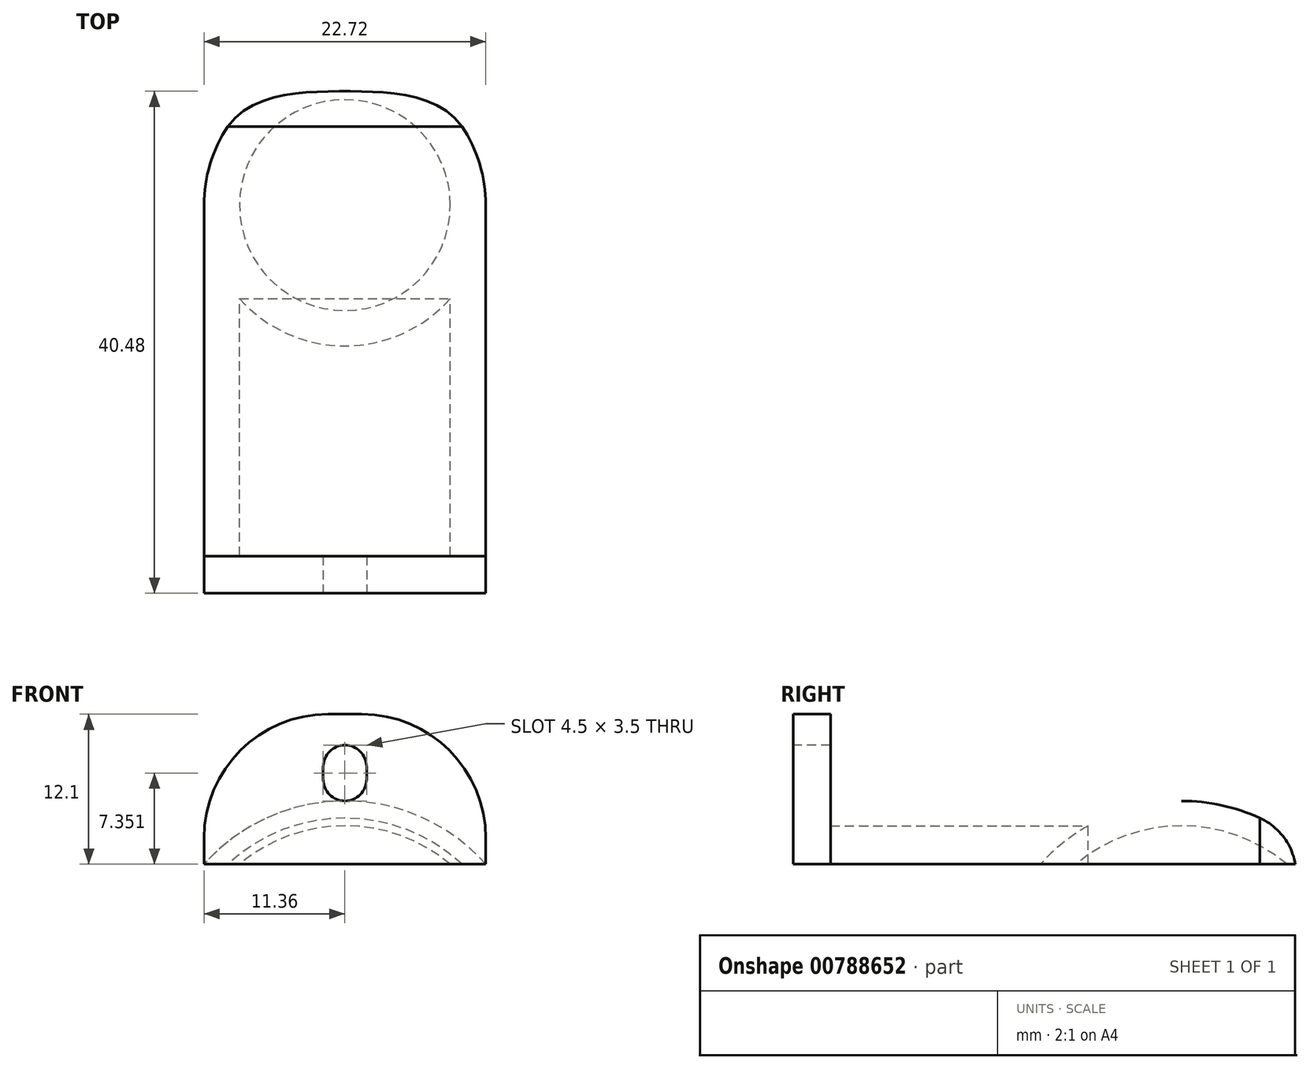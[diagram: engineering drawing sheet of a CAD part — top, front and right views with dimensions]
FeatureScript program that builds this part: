
annotation { "Feature Type Name" : "Feature", "Feature Type Description" : "" }
export const myFeature = defineFeature(function(context is Context, id is Id, definition is map)
    precondition{}
    {
        {
            var Q0;
            Q0=qCreatedBy(makeId("Front.planeOp"),FACE);
            var sketch = newSketch(context, id + "F0", { "sketchPlane" : qUnion([Q0])});
            skArc(sketch, "E0", {"start": v(8.5, 0) * mm, "mid": v(0, 3.1) * mm, "end": v(-8.5, 0) * mm});
            skLineSegment(sketch, "E1", {"start": v(-8.5, 0) * mm, "end": v(8.5, 0) * mm, "construction": true});
            skArc(sketch, "E2.0", {"start": v(11.36, 0) * mm, "mid": v(0, 5.1) * mm, "end": v(-11.36, 0) * mm});
            skLineSegment(sketch, "E3", {"start": v(-11.36, 0) * mm, "end": v(-8.5, 0) * mm});
            skLineSegment(sketch, "E4", {"start": v(8.5, 0) * mm, "end": v(11.36, 0) * mm});
            skLineSegment(sketch, "E5", {"start": v(-1.88, -10.1) * mm, "end": v(2.05, -10.1) * mm, "construction": true});
            skLineSegment(sketch, "E6.bottom", {"start": v(-11.36, 0) * mm, "end": v(11.36, 0) * mm});
            skLineSegment(sketch, "E6.top", {"start": v(-11.36, -4) * mm, "end": v(11.36, -4) * mm});
            skLineSegment(sketch, "E6.left", {"start": v(-11.36, 0) * mm, "end": v(-11.36, -4) * mm});
            skLineSegment(sketch, "E6.right", {"start": v(11.36, 0) * mm, "end": v(11.36, -4) * mm});
            skPoint(sketch, "E7", {"position": v(0, 5.1) * mm});
            skSolve(sketch);
        }
        {
            var Q0;
            Q0=makeQuery(id+"F0.imprint","IMPRINT",FACE,{"disambiguationData":[TD([[makeQuery(id+"F0.imprint","IMPRINT",EDGE,{"derivedFrom":sQuery(id+"F0.wireOp",EDGE,"E0")}),-1.0]])]});
            var Q1;
            Q1=sQuery(id+"F0.wireOp",EDGE,"E5");
            revolve(context, id + "F1", {"surfaceOperationType" : NewSurfaceOperationType.NEW, "entities" : qUnion([Q0]), "axis" : qUnion([Q1]), "revolveType" : RevolveType.SYMMETRIC, "angle" : 100 * degree});
        }
        {
            var Q0;
            Q0=makeQuery(id+"F0.imprint","IMPRINT",FACE,{"disambiguationData":[TD([[makeQuery(id+"F0.imprint","IMPRINT",EDGE,{"derivedFrom":sQuery(id+"F0.wireOp",EDGE,"E3")}),-1.0]])]});
            extrude(context, id + "F2", {"entities" : qUnion([Q0]), "operationType" : NewBodyOperationType.REMOVE, "endBound" : BoundingType.SYMMETRIC, "depth" : 25 * mm, "offsetDistance" : 25 * mm});
        }
        {
            var Q0;
            Q0=makeQuery(id+"F0.imprint","IMPRINT",FACE,{"disambiguationData":[TD([[makeQuery(id+"F0.imprint","IMPRINT",EDGE,{"derivedFrom":sQuery(id+"F0.wireOp",EDGE,"E0")}),-1.0]])]});
            extrude(context, id + "F3", {"entities" : qUnion([Q0]), "operationType" : NewBodyOperationType.ADD, "depth" : 44 * mm - 12.7 * mm, "offsetDistance" : 25 * mm});
        }
        {
            var Q0;
            Q0=qCreatedBy(makeId("Top.planeOp"),FACE);
            var sketch = newSketch(context, id + "F4", { "sketchPlane" : qUnion([Q0])});
            skLineSegment(sketch, "E8.bottom", {"start": v(-11.36, -31.3) * mm, "end": v(11.36, -31.3) * mm});
            skLineSegment(sketch, "E8.top", {"start": v(-11.36, -28.3) * mm, "end": v(11.36, -28.3) * mm});
            skLineSegment(sketch, "E8.left", {"start": v(-11.36, -31.3) * mm, "end": v(-11.36, -28.3) * mm});
            skLineSegment(sketch, "E8.right", {"start": v(11.36, -31.3) * mm, "end": v(11.36, -28.3) * mm});
            skSolve(sketch);
        }
        {
            var Q0;
            Q0=makeQuery(id+"F4.imprint","IMPRINT",FACE,{"disambiguationData":[TD([[makeQuery(id+"F4.imprint","IMPRINT",EDGE,{"derivedFrom":sQuery(id+"F4.wireOp",EDGE,"E8.bottom")}),1.0]])]});
            extrude(context, id + "F5", {"entities" : qUnion([Q0]), "operationType" : NewBodyOperationType.ADD, "depth" : 5.1 * mm + 7 * mm, "offsetDistance" : 25 * mm});
        }
        {
            var Q0;
            Q0=makeQuery(id+"F5.boolean.opBoolean","MERGE",FACE,{"derivedFrom":[makeQuery(id+"F3.opExtrude","CAP_FACE",FACE,{"disambiguationData":[OSD([sQuery(id+"F0.wireOp",EDGE,"E0"),sQuery(id+"F0.wireOp",EDGE,"E2.0"),sQuery(id+"F0.wireOp",EDGE,"E3"),sQuery(id+"F0.wireOp",EDGE,"E4")])],"isStart":false}),makeQuery(id+"F5.opExtrude","SWEPT_FACE",FACE,{"disambiguationData":[OSD([sQuery(id+"F4.wireOp",EDGE,"E8.bottom")])]})]});
            var sketch = newSketch(context, id + "F6", { "sketchPlane" : qUnion([Q0])});
            skArc(sketch, "E9", {"start": v(1.75, 7.85) * mm, "mid": v(0, 9.6) * mm, "end": v(-1.75, 7.85) * mm});
            skArc(sketch, "E10", {"start": v(-1.75, 6.85) * mm, "mid": v(0, 5.1) * mm, "end": v(1.75, 6.85) * mm});
            skLineSegment(sketch, "E11", {"start": v(-1.75, 7.85) * mm, "end": v(-1.75, 6.85) * mm});
            skLineSegment(sketch, "E12", {"start": v(1.75, 7.85) * mm, "end": v(1.75, 6.85) * mm});
            skSolve(sketch);
        }
        {
            var Q0;
            Q0=makeQuery(id+"F6.imprint","IMPRINT",FACE,{"disambiguationData":[TD([[makeQuery(id+"F6.imprint","IMPRINT",EDGE,{"derivedFrom":sQuery(id+"F6.wireOp",EDGE,"E9")}),1.0]])]});
            extrude(context, id + "F7", {"entities" : qUnion([Q0]), "operationType" : NewBodyOperationType.REMOVE, "endBound" : BoundingType.THROUGH_ALL, "oppositeDirection" : true, "depth" : 25 * mm, "offsetDistance" : 25 * mm});
        }
        {
            var Q0;
            Q0=makeQuery(id+"F5.opExtrude","CAP_EDGE",EDGE,{"disambiguationData":[OSD([sQuery(id+"F4.wireOp",EDGE,"E8.left")])],"isStart":false});
            var Q1;
            Q1=makeQuery(id+"F5.opExtrude","CAP_EDGE",EDGE,{"disambiguationData":[OSD([sQuery(id+"F4.wireOp",EDGE,"E8.right")])],"isStart":false});
            fillet(context, id + "F8", {"entities" : qUnion([Q0, Q1]), "radius" : 10 * mm, "tangentPropagation" : true, "allowEdgeOverflow" : false});
        }
        {
            var Q0;
            Q0=qCreatedBy(makeId("Top.planeOp"),FACE);
            var sketch = newSketch(context, id + "F9", { "sketchPlane" : qUnion([Q0])});
            skLineSegment(sketch, "E13.bottom", {"start": v(-6.6, 11.36) * mm, "end": v(6.6, 11.36) * mm});
            skLineSegment(sketch, "E13.top", {"start": v(-6.6, 9.25) * mm, "end": v(6.6, 9.25) * mm});
            skLineSegment(sketch, "E13.left", {"start": v(-6.6, 11.36) * mm, "end": v(-6.6, 9.25) * mm});
            skLineSegment(sketch, "E13.right", {"start": v(6.6, 11.36) * mm, "end": v(6.6, 9.25) * mm});
            skSolve(sketch);
        }
        {
            var Q0;
            Q0=makeQuery(id+"F9.imprint","IMPRINT",FACE,{"disambiguationData":[TD([[makeQuery(id+"F9.imprint","IMPRINT",EDGE,{"derivedFrom":sQuery(id+"F9.wireOp",EDGE,"E13.bottom")}),-1.0]])]});
            extrude(context, id + "F10", {"entities" : qUnion([Q0]), "operationType" : NewBodyOperationType.REMOVE, "depth" : 25 * mm, "offsetDistance" : 25 * mm});
        }
        {
            var Q0;
            {var subQ2=sQuery(id+"F0.wireOp",EDGE,"E2.0");Q0=makeQuery(id+"F10.boolean.opBoolean","INTERSECT",EDGE,{"derivedFrom":[makeQuery(id+"F3.boolean.opBoolean","SPLIT",FACE,{"disambiguationData":[TD([makeQuery(id+"F3.opExtrude","SWEPT_FACE",FACE,{"disambiguationData":[OSD([subQ2])]})])],"derivedFrom":makeQuery(id+"F1.opRevolve","SWEPT_FACE",FACE,{"disambiguationData":[OSD([subQ2])]})}),makeQuery(id+"F10.opExtrude","SWEPT_FACE",FACE,{"disambiguationData":[OSD([sQuery(id+"F9.wireOp",EDGE,"E13.top")])]})]});}
            fillet(context, id + "F11", {"entities" : qUnion([Q0]), "radius" : 5 * mm, "tangentPropagation" : true, "allowEdgeOverflow" : false});
        }
    });
